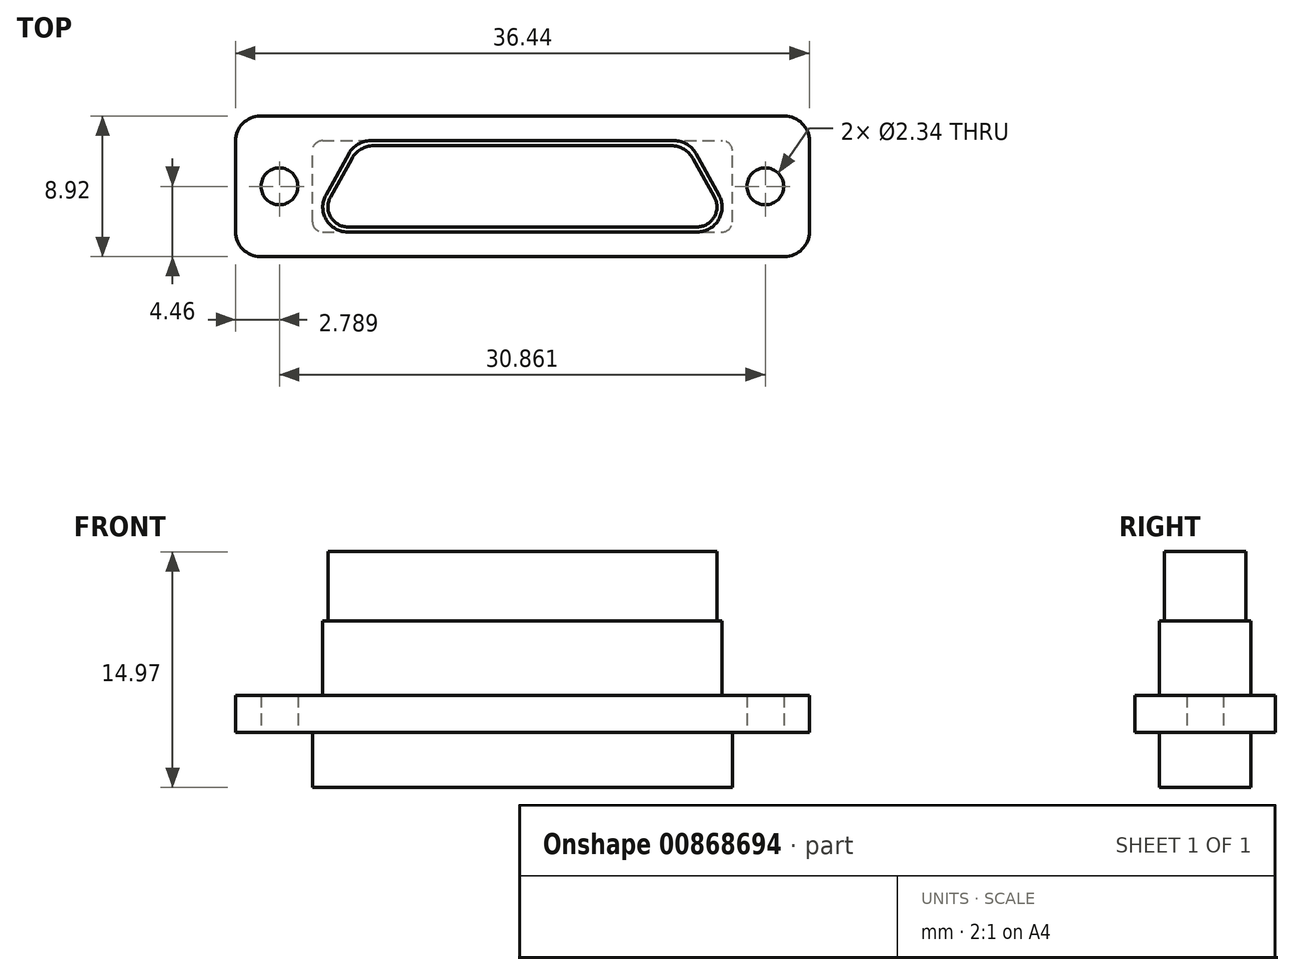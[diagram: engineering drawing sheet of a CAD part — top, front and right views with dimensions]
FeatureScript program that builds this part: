
annotation { "Feature Type Name" : "Feature", "Feature Type Description" : "" }
export const myFeature = defineFeature(function(context is Context, id is Id, definition is map)
    precondition{}
    {
        {
            var Q0;
            Q0=qCreatedBy(makeId("Top.planeOp"),FACE);
            var sketch = newSketch(context, id + "F0", { "sketchPlane" : qUnion([Q0])});
            skLineSegment(sketch, "E0.bottom", {"start": v(-16.65, 4.46) * mm, "end": v(16.65, 4.46) * mm});
            skLineSegment(sketch, "E0.top", {"start": v(-16.65, -4.46) * mm, "end": v(16.65, -4.46) * mm});
            skLineSegment(sketch, "E0.left", {"start": v(-18.22, 2.88) * mm, "end": v(-18.22, -2.88) * mm});
            skLineSegment(sketch, "E0.right", {"start": v(18.22, 2.88) * mm, "end": v(18.22, -2.88) * mm});
            skPoint(sketch, "E0.middle", {"position": v(0, 0) * mm});
            skCircle(sketch, "E1", {"center": v(-15.43, 0) * mm, "radius": 1.17 * mm});
            skCircle(sketch, "E2", {"center": v(15.43, 0) * mm, "radius": 1.17 * mm});
            skPoint(sketch, "E3.visualSharp", {"position": v(-18.22, -4.46) * mm});
            skArc(sketch, "E3.filletArc", {"start": v(-18.22, -2.88) * mm, "mid": v(-17.76, -4) * mm, "end": v(-16.65, -4.46) * mm});
            skPoint(sketch, "E4.visualSharp", {"position": v(-18.22, 4.46) * mm});
            skArc(sketch, "E4.filletArc", {"start": v(-16.65, 4.46) * mm, "mid": v(-17.76, 4) * mm, "end": v(-18.22, 2.88) * mm});
            skPoint(sketch, "E5.visualSharp", {"position": v(18.22, 4.46) * mm});
            skArc(sketch, "E5.filletArc", {"start": v(18.22, 2.88) * mm, "mid": v(17.76, 4) * mm, "end": v(16.65, 4.46) * mm});
            skPoint(sketch, "E6.visualSharp", {"position": v(18.22, -4.46) * mm});
            skArc(sketch, "E6.filletArc", {"start": v(16.65, -4.46) * mm, "mid": v(17.76, -4) * mm, "end": v(18.22, -2.88) * mm});
            skSolve(sketch);
        }
        {
            var Q0;
            Q0=makeQuery(id+"F0.imprint","IMPRINT",FACE,{"disambiguationData":[TD([[makeQuery(id+"F0.imprint","IMPRINT",EDGE,{"derivedFrom":sQuery(id+"F0.wireOp",EDGE,"E0.bottom")}),-1.0]])]});
            extrude(context, id + "F1", {"entities" : qUnion([Q0]), "endBound" : BoundingType.SYMMETRIC, "depth" : 2.36 * mm, "offsetDistance" : 25.4 * mm});
        }
        {
            var Q0;
            Q0=makeQuery(id+"F1.opExtrude","CAP_FACE",FACE,{"disambiguationData":[OSD([sQuery(id+"F0.wireOp",EDGE,"E0.bottom"),sQuery(id+"F0.wireOp",EDGE,"E0.top"),sQuery(id+"F0.wireOp",EDGE,"E0.left"),sQuery(id+"F0.wireOp",EDGE,"E0.right"),sQuery(id+"F0.wireOp",EDGE,"E1"),sQuery(id+"F0.wireOp",EDGE,"E2"),sQuery(id+"F0.wireOp",EDGE,"E3.filletArc"),sQuery(id+"F0.wireOp",EDGE,"E4.filletArc"),sQuery(id+"F0.wireOp",EDGE,"E5.filletArc"),sQuery(id+"F0.wireOp",EDGE,"E6.filletArc")])],"isStart":false});
            var sketch = newSketch(context, id + "F2", { "sketchPlane" : qUnion([Q0])});
            skPoint(sketch, "E7.middle", {"position": v(0, 0) * mm});
            skLineSegment(sketch, "E8.top", {"start": v(11.1, -2.9) * mm, "end": v(-11.1, -2.9) * mm});
            skLineSegment(sketch, "E9", {"start": v(-9.64, 2.9) * mm, "end": v(9.64, 2.9) * mm});
            skLineSegment(sketch, "E10", {"start": v(-12.48, -0.56) * mm, "end": v(-11.02, 2.08) * mm});
            skLineSegment(sketch, "E11", {"start": v(11.02, 2.08) * mm, "end": v(12.48, -0.56) * mm});
            skPoint(sketch, "E12.visualSharp", {"position": v(-10.57, 2.9) * mm});
            skArc(sketch, "E12.filletArc", {"start": v(-9.64, 2.9) * mm, "mid": v(-10.44, 2.68) * mm, "end": v(-11.02, 2.08) * mm});
            skPoint(sketch, "E13.visualSharp", {"position": v(-13.78, -2.9) * mm});
            skArc(sketch, "E13.filletArc", {"start": v(-12.48, -0.56) * mm, "mid": v(-12.46, -2.12) * mm, "end": v(-11.1, -2.9) * mm});
            skPoint(sketch, "E14.visualSharp", {"position": v(13.78, -2.9) * mm});
            skArc(sketch, "E14.filletArc", {"start": v(11.1, -2.9) * mm, "mid": v(12.46, -2.12) * mm, "end": v(12.48, -0.56) * mm});
            skPoint(sketch, "E15.visualSharp", {"position": v(10.57, 2.9) * mm});
            skArc(sketch, "E15.filletArc", {"start": v(11.02, 2.08) * mm, "mid": v(10.44, 2.68) * mm, "end": v(9.64, 2.9) * mm});
            skSolve(sketch);
        }
        {
            var Q0;
            Q0 = qSketchRegion(id + "F2", true);
            extrude(context, id + "F3", {"entities" : qUnion([Q0]), "operationType" : NewBodyOperationType.ADD, "depth" : 4.72 * mm, "offsetDistance" : 25.4 * mm});
        }
        {
            var Q0;
            Q0=makeQuery(id+"F1.opExtrude","CAP_FACE",FACE,{"disambiguationData":[OSD([sQuery(id+"F0.wireOp",EDGE,"E0.bottom"),sQuery(id+"F0.wireOp",EDGE,"E0.top"),sQuery(id+"F0.wireOp",EDGE,"E0.left"),sQuery(id+"F0.wireOp",EDGE,"E0.right"),sQuery(id+"F0.wireOp",EDGE,"E1"),sQuery(id+"F0.wireOp",EDGE,"E2"),sQuery(id+"F0.wireOp",EDGE,"E3.filletArc"),sQuery(id+"F0.wireOp",EDGE,"E4.filletArc"),sQuery(id+"F0.wireOp",EDGE,"E5.filletArc"),sQuery(id+"F0.wireOp",EDGE,"E6.filletArc")])],"isStart":true});
            var sketch = newSketch(context, id + "F4", { "sketchPlane" : qUnion([Q0])});
            skLineSegment(sketch, "E16.bottom", {"start": v(-12.7, 2.9) * mm, "end": v(12.7, 2.9) * mm});
            skLineSegment(sketch, "E16.top", {"start": v(-12.7, -2.9) * mm, "end": v(12.7, -2.9) * mm});
            skLineSegment(sketch, "E16.left", {"start": v(-13.34, 2.26) * mm, "end": v(-13.34, -2.26) * mm});
            skLineSegment(sketch, "E16.right", {"start": v(13.34, 2.26) * mm, "end": v(13.34, -2.26) * mm});
            skPoint(sketch, "E16.middle", {"position": v(0, 0) * mm});
            skPoint(sketch, "E17.visualSharp", {"position": v(-13.34, 2.9) * mm});
            skArc(sketch, "E17.filletArc", {"start": v(-12.7, 2.9) * mm, "mid": v(-13.15, 2.7) * mm, "end": v(-13.34, 2.26) * mm});
            skPoint(sketch, "E18.visualSharp", {"position": v(-13.34, -2.9) * mm});
            skArc(sketch, "E18.filletArc", {"start": v(-13.34, -2.26) * mm, "mid": v(-13.15, -2.7) * mm, "end": v(-12.7, -2.9) * mm});
            skPoint(sketch, "E19.visualSharp", {"position": v(13.34, -2.9) * mm});
            skArc(sketch, "E19.filletArc", {"start": v(12.7, -2.9) * mm, "mid": v(13.15, -2.7) * mm, "end": v(13.34, -2.26) * mm});
            skPoint(sketch, "E20.visualSharp", {"position": v(13.34, 2.9) * mm});
            skArc(sketch, "E20.filletArc", {"start": v(13.34, 2.26) * mm, "mid": v(13.15, 2.7) * mm, "end": v(12.7, 2.9) * mm});
            skSolve(sketch);
        }
        {
            var Q0;
            Q0 = qSketchRegion(id + "F4", true);
            extrude(context, id + "F5", {"entities" : qUnion([Q0]), "operationType" : NewBodyOperationType.ADD, "depth" : 3.48 * mm, "offsetDistance" : 25.4 * mm});
        }
        {
            var Q0;
            Q0=makeQuery(id+"F3.opExtrude","CAP_FACE",FACE,{"disambiguationData":[OSD([sQuery(id+"F2.wireOp",EDGE,"E8.top"),sQuery(id+"F2.wireOp",EDGE,"E9"),sQuery(id+"F2.wireOp",EDGE,"E10"),sQuery(id+"F2.wireOp",EDGE,"E11"),sQuery(id+"F2.wireOp",EDGE,"E12.filletArc"),sQuery(id+"F2.wireOp",EDGE,"E13.filletArc"),sQuery(id+"F2.wireOp",EDGE,"E14.filletArc"),sQuery(id+"F2.wireOp",EDGE,"E15.filletArc")])],"isStart":false});
            var sketch = newSketch(context, id + "F6", { "sketchPlane" : qUnion([Q0])});
            skLineSegment(sketch, "E21", {"start": v(-9.45, 2.58) * mm, "end": v(9.46, 2.58) * mm});
            skLineSegment(sketch, "E22", {"start": v(10.83, 1.77) * mm, "end": v(12.2, -0.7) * mm});
            skLineSegment(sketch, "E23", {"start": v(11.09, -2.58) * mm, "end": v(-11.08, -2.58) * mm});
            skLineSegment(sketch, "E24", {"start": v(-12.2, -0.7) * mm, "end": v(-10.83, 1.77) * mm});
            skPoint(sketch, "E25.visualSharp", {"position": v(-13.24, -2.58) * mm});
            skArc(sketch, "E25.filletArc", {"start": v(-12.2, -0.7) * mm, "mid": v(-12.18, -1.95) * mm, "end": v(-11.08, -2.58) * mm});
            skPoint(sketch, "E26.visualSharp", {"position": v(-10.38, 2.58) * mm});
            skArc(sketch, "E26.filletArc", {"start": v(-9.45, 2.58) * mm, "mid": v(-10.25, 2.36) * mm, "end": v(-10.83, 1.77) * mm});
            skPoint(sketch, "E27.visualSharp", {"position": v(10.38, 2.58) * mm});
            skArc(sketch, "E27.filletArc", {"start": v(10.83, 1.77) * mm, "mid": v(10.26, 2.36) * mm, "end": v(9.46, 2.58) * mm});
            skPoint(sketch, "E28.visualSharp", {"position": v(13.24, -2.58) * mm});
            skArc(sketch, "E28.filletArc", {"start": v(11.09, -2.58) * mm, "mid": v(12.18, -1.95) * mm, "end": v(12.2, -0.7) * mm});
            skSolve(sketch);
        }
        {
            var Q0;
            Q0 = qSketchRegion(id + "F6", true);
            extrude(context, id + "F7", {"entities" : qUnion([Q0]), "operationType" : NewBodyOperationType.ADD, "oppositeDirection" : true, "depth" : -4.4 * mm, "offsetDistance" : 25.4 * mm});
        }
    });
